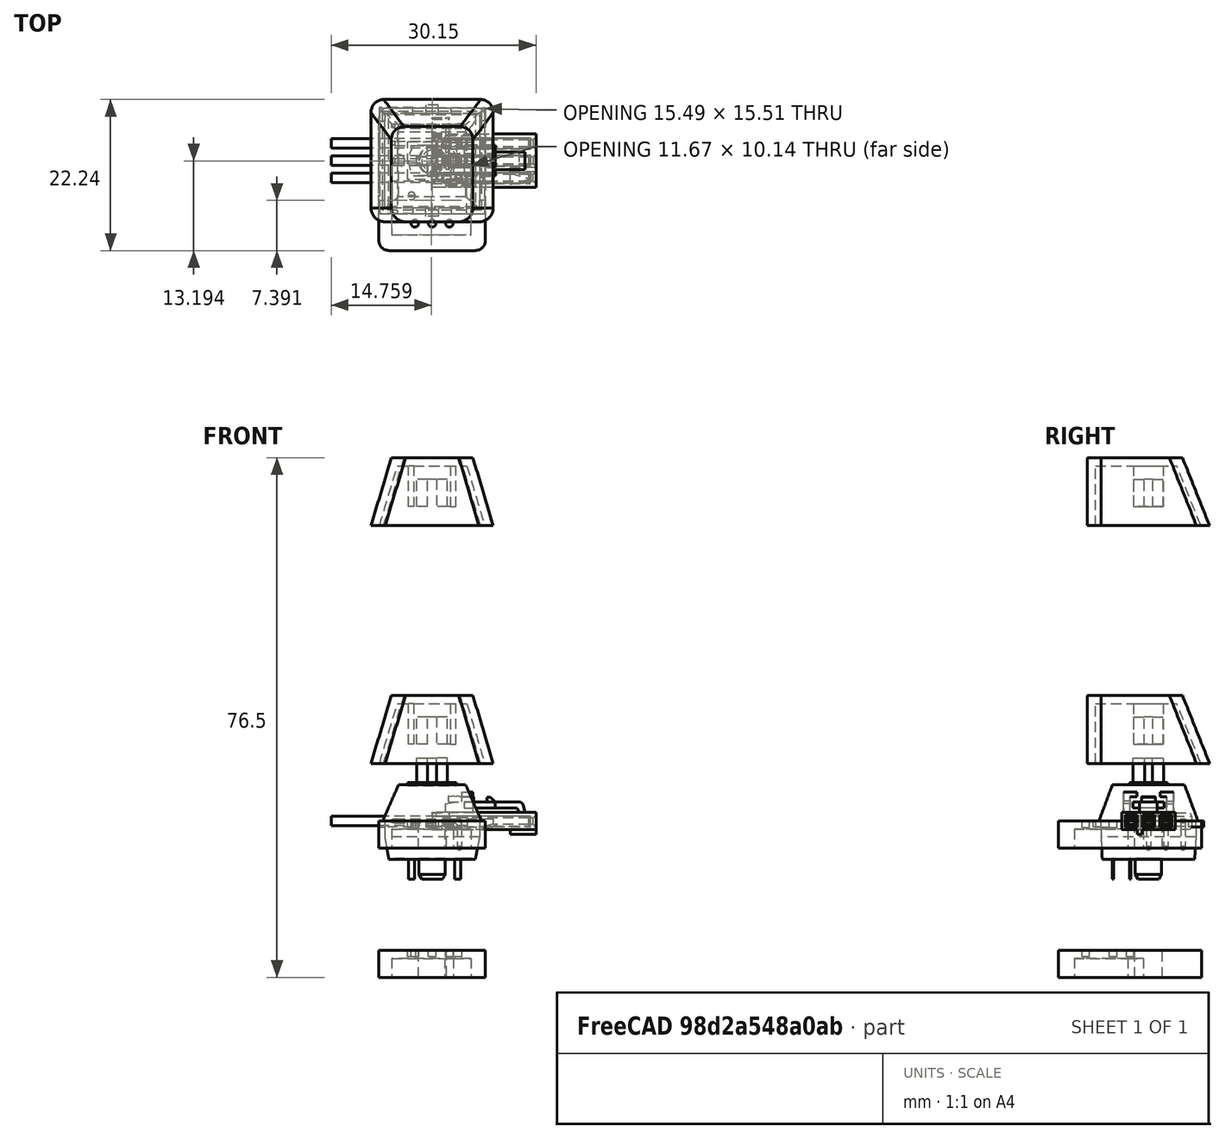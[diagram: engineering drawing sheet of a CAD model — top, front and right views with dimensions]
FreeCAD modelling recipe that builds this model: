
FCSTD DOCUMENT  (FreeCAD 0.19R19285 (Git))
Label: pcbprint-cherry-mx
Comment: 3D-parts by Obijuan -- https://github.com/Obijuan/3D-parts
License: Creative Commons Attribution-ShareAlike
LicenseURL: http://creativecommons.org/licenses/by-sa/4.0/
objects: Part::Feature×36, Part::Part2DObjectPython×33, App::Part×8, Sketcher::SketchObject×6, App::Annotation×5, App::DocumentObjectGroup×4, PartDesign::Pad×2, PartDesign::Pocket×2, PartDesign::Plane×1, PartDesign::Fillet×1, PartDesign::Body×1, Mesh::Feature×1
note: 86 computed .brp shape members not serialized (recipe doc carries the construction recipe); baked Part::Feature solids carry a one-line shape summary decoded from their .brp

FEATURE [Sketcher::SketchObject] Sketch  label="master_h"
  MapMode = 5
  Support = -> [XY_Plane]
  expr: Constraints[1] = 3.8500000000000001 + 0.20000000000000001
  sketch-geometry (14):
    g0: Circle CenterX=0 CenterY=0 CenterZ=0 NormalX=0 NormalY=0 NormalZ=1 AngleXU=0 Radius=2.025
    g1: GeomPoint X=-3.03 Y=-5.2 Z=0
    g2: Circle CenterX=-3.03 CenterY=-5.2 CenterZ=0 NormalX=0 NormalY=0 NormalZ=1 AngleXU=0 Radius=0.55
    g3: GeomPoint X=3.77 Y=-2.7 Z=0
    g4: Circle CenterX=3.77 CenterY=-2.7 CenterZ=0 NormalX=0 NormalY=0 NormalZ=1 AngleXU=0 Radius=0.55
    g5: LineSegment StartX=-7.8514 StartY=7.82934 StartZ=0 EndX=7.8514 EndY=7.82934 EndZ=0
    g6: LineSegment StartX=7.8514 StartY=7.82934 StartZ=0 EndX=7.8514 EndY=-13.2357 EndZ=0
    g7: LineSegment StartX=7.8514 StartY=-13.2357 StartZ=0 EndX=-7.8514 EndY=-13.2357 EndZ=0
    g8: LineSegment StartX=-7.8514 StartY=-13.2357 StartZ=0 EndX=-7.8514 EndY=7.82934 EndZ=0
    g9: Circle CenterX=0 CenterY=-9.23 CenterZ=0 NormalX=0 NormalY=0 NormalZ=1 AngleXU=0 Radius=0.55
    g10: Circle CenterX=2.54 CenterY=-9.23 CenterZ=0 NormalX=0 NormalY=0 NormalZ=1 AngleXU=0 Radius=0.55
    g11: LineSegment [constr] StartX=0 StartY=-9.23 StartZ=0 EndX=2.54 EndY=-9.23 EndZ=0
    g12: Circle CenterX=-2.54 CenterY=-9.23 CenterZ=0 NormalX=0 NormalY=0 NormalZ=1 AngleXU=0 Radius=0.55
    g13: LineSegment [constr] StartX=-2.54 StartY=-9.23 StartZ=0 EndX=0 EndY=-9.23 EndZ=0
  constraints (31):
    c: Coincident(g0,g-1)
    c: Diameter(g0) = 4.05
    c: DistanceX(g1,g0) = 3.03
    c: DistanceY(g1,g0) = 5.2
    c: Coincident(g2,g1)
    c: Diameter(g2) = 1.1
    c: DistanceY(g3,g0) = 2.7
    c: DistanceX(g0,g3) = 3.77
    c: Coincident(g4,g3)
    c: Equal(g2,g4)
    c: Coincident(g5,g6)
    c: Coincident(g6,g7)
    c: Coincident(g7,g8)
    c: Coincident(g8,g5)
    c: Horizontal(g7)
    c: Vertical(g6)
    c: Vertical(g8)
    c: Equal(g2,g9)
    c: PointOnObject(g9,g-2)
    c: DistanceY(g9,g0) = 9.23
    c: Equal(g9,g10)
    c: Coincident(g11,g9)
    c: Coincident(g11,g10)
    c: Horizontal(g11)
    c: DistanceX(g11,g11) = 2.54
    c: Equal(g12,g9)
    c: PointOnObject(g12,g11)
    c: Coincident(g13,g12)
    c: Coincident(g13,g9)
    c: Equal(g13,g11)
    c: Symmetric(g5,g5,g-2)
FEATURE [Sketcher::SketchObject] Sketch001  label="master_v"
  MapMode = 5
  Placement = pos=(0,0,0) rot=(1,0,0;1.5708rad)
  Support = -> [XZ_Plane]
  sketch-geometry (2):
    g0: LineSegment StartX=0 StartY=0 StartZ=0 EndX=0 EndY=-1 EndZ=0
    g1: LineSegment StartX=0 StartY=-1 StartZ=0 EndX=0 EndY=-4 EndZ=0
  constraints (6):
    c: Coincident(g0,g-1)
    c: PointOnObject(g0,g-2)
    c: DistanceY(g0,g0) = 1  'h1'
    c: Coincident(g1,g0)
    c: Vertical(g1)
    c: DistanceY(g1,g1) = 3  'h2'
FEATURE [Sketcher::SketchObject] Sketch002  label="botom_1_sk"
  ExternalGeometry = -> [Sketch]
  MapMode = 5
  Support = -> [XY_Plane]
  sketch-geometry (4):
    g0: LineSegment StartX=-7.8514 StartY=7.82934 StartZ=0 EndX=7.8514 EndY=7.82934 EndZ=0
    g1: LineSegment StartX=7.8514 StartY=7.82934 StartZ=0 EndX=7.8514 EndY=-13.2357 EndZ=0
    g2: LineSegment StartX=7.8514 StartY=-13.2357 StartZ=0 EndX=-7.8514 EndY=-13.2357 EndZ=0
    g3: LineSegment StartX=-7.8514 StartY=-13.2357 StartZ=0 EndX=-7.8514 EndY=7.82934 EndZ=0
  constraints (10):
    c: Coincident(g0,g1)
    c: Coincident(g1,g2)
    c: Coincident(g2,g3)
    c: Coincident(g3,g0)
    c: Horizontal(g0)
    c: Horizontal(g2)
    c: Vertical(g1)
    c: Vertical(g3)
    c: Coincident(g-3,g0)
    c: Coincident(g1,g-4)
FEATURE [PartDesign::Pad] Pad  label="bottom-body"
  Length = 4
  Length2 = 100
  Profile = -> Sketch002
  Refine = true
  Reversed = true
  Type = 0
  expr: Length = <<master_v>>.Constraints.h1 + <<master_v>>.Constraints.h2
FEATURE [Sketcher::SketchObject] Sketch003  label="drills_sk"
  ExternalGeometry = -> [Sketch]
  MapMode = 5
  Support = -> [XY_Plane]
  expr: Constraints[1] = Sketch.Constraints[1]
  expr: Constraints[2] = Sketch.Constraints[2]
  expr: Constraints[5] = Sketch.Constraints[5]
  expr: Constraints[3] = Sketch.Constraints[3]
  expr: Constraints[6] = Sketch.Constraints[6]
  expr: Constraints[7] = Sketch.Constraints[7]
  sketch-geometry (8):
    g0: Circle CenterX=0 CenterY=0 CenterZ=0 NormalX=0 NormalY=0 NormalZ=1 AngleXU=0 Radius=2.025
    g1: GeomPoint X=-3.03 Y=-5.2 Z=0
    g2: Circle CenterX=-3.03 CenterY=-5.2 CenterZ=0 NormalX=0 NormalY=0 NormalZ=1 AngleXU=0 Radius=0.55
    g3: GeomPoint X=3.77 Y=-2.7 Z=0
    g4: Circle CenterX=3.77 CenterY=-2.7 CenterZ=0 NormalX=0 NormalY=0 NormalZ=1 AngleXU=0 Radius=0.55
    g5: Circle CenterX=-2.54 CenterY=-9.23 CenterZ=0 NormalX=0 NormalY=0 NormalZ=1 AngleXU=0 Radius=0.55
    g6: Circle CenterX=0 CenterY=-9.23 CenterZ=0 NormalX=0 NormalY=0 NormalZ=1 AngleXU=0 Radius=0.55
    g7: Circle CenterX=2.54 CenterY=-9.23 CenterZ=0 NormalX=0 NormalY=0 NormalZ=1 AngleXU=0 Radius=0.55
  constraints (16):
    c: Coincident(g0,g-1)
    c: Diameter(g0) = 4.05
    c: DistanceX(g1,g0) = 3.03
    c: DistanceY(g1,g0) = 5.2
    c: Coincident(g2,g1)
    c: Diameter(g2) = 1.1
    c: DistanceY(g3,g0) = 2.7
    c: DistanceX(g0,g3) = 3.77
    c: Coincident(g4,g3)
    c: Equal(g2,g4)
    c: Coincident(g-5,g7)
    c: Equal(g7,g-5)
    c: Coincident(g6,g-4)
    c: Equal(g6,g-4)
    c: Coincident(g5,g-3)
    c: Equal(g5,g-3)
FEATURE [PartDesign::Pocket] Pocket  label="drills-cutout"
  BaseFeature = -> Pad
  Length = 5
  Length2 = 100
  Profile = -> Sketch003
  Refine = true
  Type = 1
FEATURE [Part::Feature] Part__Feature  label="1x3-Insulator"
  shape: bbox 2.54 x 7.62 x 2.5 mm, 30 faces (baked)
FEATURE [Part::Feature] Part__Feature001  label="pin"
  shape: bbox 10.36 x 0.64 x 4.57 mm, 18 faces (baked)
FEATURE [Part::Feature] Part__Feature002  label="pin2"
  Placement = pos=(0,2.54,0) rot=(0,0,1;0rad)
  shape: bbox 10.36 x 0.64 x 4.57 mm, 18 faces (baked)
FEATURE [Part::Feature] Part__Feature003  label="pin3"
  Placement = pos=(0,5.08,0) rot=(0,0,1;0rad)
  shape: bbox 10.36 x 0.64 x 4.57 mm, 18 faces (baked)
FEATURE [App::Part] _x3_mape_pin_header_right_angle  label="1x3-mape-pin-header-right-angle"
  Group = -> [Part__Feature,Part__Feature001,Part__Feature002,Part__Feature003]
  Origin = -> Origin001
  Placement = pos=(2.55,-13.25,1.25) rot=(0,0,1;1.5708rad)
FEATURE [Part::Feature] Part__Feature004  label="cherry-body"
  shape: bbox 15.64 x 16.33 x 10.95 mm, 75 faces (baked)
FEATURE [Part::Feature] Part__Feature005  label="cherry-axis"
  Placement = pos=(0,0,5.25) rot=(0,0,1;0rad)
  shape: bbox 7.2 x 5.56 x 4.05 mm, 19 faces (baked)
FEATURE [Part::Feature] Part__Feature006  label="cherry-peg"
  Placement = pos=(0,0,-8.55) rot=(0,0,1;0rad)
  shape: bbox 3.85 x 3.85 x 3.05 mm, 4 faces (baked)
FEATURE [Part::Feature] Part__Feature007  label="pin1"
  Placement = pos=(-3.03,-5.2,-8.55) rot=(0,0,1;0rad)
  shape: bbox 0.86 x 0.2 x 3.05 mm, 6 faces (baked)
FEATURE [Part::Feature] Part__Feature008  label="pin004"
  Placement = pos=(3.77,-2.7,-8.55) rot=(0,0,1;0rad)
  shape: bbox 0.86 x 0.2 x 3.05 mm, 6 faces (baked)
FEATURE [App::Part] cherry_mx_basic  label="cherry-mx-basic"
  Group = -> [Part__Feature004,Part__Feature005,Part__Feature006,Part__Feature007,Part__Feature008]
  Origin = -> Origin002
  Placement = pos=(0,0,5.6) rot=(0,0,1;0rad)
FEATURE [Part::Feature] Part__Feature016  label="Connector"
  shape: bbox 15.3 x 7.9 x 6.24 mm, 133 faces (baked)
FEATURE [Part::Feature] Part__Feature017  label="pins"
  shape: bbox 12.6 x 1.5 x 1.959 mm, 26 faces (baked)
FEATURE [Part::Feature] Part__Feature018  label="pins001"
  shape: bbox 12.6 x 1.5 x 1.959 mm, 26 faces (baked)
FEATURE [Part::Feature] Part__Feature019  label="pins002"
  shape: bbox 12.6 x 1.5 x 1.959 mm, 26 faces (baked)
FEATURE [App::Part] pins  label="pins003"
  Group = -> [Part__Feature017,Part__Feature018,Part__Feature019]
  Origin = -> Origin004
FEATURE [Part::Feature] Part__Feature020  label="vcc-wire001"
  Placement = pos=(5.15,0,0) rot=(0,-1,0;1.5708rad)
  shape: bbox 20 x 1.4 x 1.4 mm, 3 faces (baked)
FEATURE [Part::Feature] Part__Feature021  label="vcc-signal001"
  Placement = pos=(5.15,2.54,0) rot=(0,-1,0;1.5708rad)
  shape: bbox 20 x 1.4 x 1.4 mm, 3 faces (baked)
FEATURE [Part::Feature] Part__Feature022  label="wire-gnd001"
  Placement = pos=(5.15,-2.54,0) rot=(0,-1,0;1.5708rad)
  shape: bbox 20 x 1.4 x 1.4 mm, 3 faces (baked)
FEATURE [App::Part] ASSEMBLY001  label="female-connector"
  Group = -> [Part__Feature016,pins,Part__Feature020,Part__Feature021,Part__Feature022]
  Origin = -> Origin005
  Placement = pos=(-6.4e-15,-28.7,1.25) rot=(0,0,1;1.5708rad)
FEATURE [PartDesign::Plane] DatumPlane  label="First-layer"
  AttachmentOffset = pos=(0,0,-1) rot=(0,0,1;0rad)
  Length = 60
  MapMode = 2
  Placement = pos=(0,0,-1) rot=(0,0,1;0rad)
  ResizeMode = 0
  Support = -> [XY_Plane]
  Width = 60
FEATURE [Sketcher::SketchObject] Sketch004  label="tracks-sk"
  MapMode = 5
  Placement = pos=(0,0,-1) rot=(0,0,1;0rad)
  Support = -> [DatumPlane]
  sketch-geometry (6):
    g0: LineSegment StartX=-5.92823 StartY=-3.06635 StartZ=0 EndX=1.85452 EndY=-3.06635 EndZ=0
    g1: LineSegment StartX=1.85452 StartY=-3.06635 StartZ=0 EndX=3.12806 EndY=-0.77869 EndZ=0
    g2: LineSegment StartX=3.12806 StartY=-0.77869 StartZ=0 EndX=5.7459 EndY=-0.77869 EndZ=0
    g3: LineSegment StartX=5.7459 StartY=-0.77869 StartZ=0 EndX=5.7459 EndY=-10.9199 EndZ=0
    g4: LineSegment StartX=5.7459 StartY=-10.9199 StartZ=0 EndX=-5.92823 EndY=-10.9199 EndZ=0
    g5: LineSegment StartX=-5.92823 StartY=-10.9199 StartZ=0 EndX=-5.92823 EndY=-3.06635 EndZ=0
  constraints (11):
    c: Horizontal(g0)
    c: Coincident(g0,g1)
    c: Coincident(g1,g2)
    c: Horizontal(g2)
    c: Coincident(g2,g3)
    c: Vertical(g3)
    c: Coincident(g3,g4)
    c: Horizontal(g4)
    c: Coincident(g4,g5)
    c: Coincident(g5,g0)
    c: Vertical(g5)
FEATURE [PartDesign::Pocket] Pocket001  label="tracks-cutout"
  BaseFeature = -> Pocket
  Length = 5
  Length2 = 100
  Profile = -> Sketch004
  Refine = true
  Type = 1
FEATURE [Sketcher::SketchObject] Sketch005  label="drills-fill-sk"
  ExternalGeometry = -> [Sketch004]
  MapMode = 5
  Placement = pos=(0,0,-1) rot=(0,0,1;0rad)
  Support = -> [DatumPlane]
  sketch-geometry (6):
    g0: LineSegment StartX=-5.92823 StartY=-3.06635 StartZ=0 EndX=1.85452 EndY=-3.06635 EndZ=0
    g1: LineSegment StartX=1.85452 StartY=-3.06635 StartZ=0 EndX=3.12806 EndY=-0.77869 EndZ=0
    g2: LineSegment StartX=3.12806 StartY=-0.77869 StartZ=0 EndX=5.7459 EndY=-0.77869 EndZ=0
    g3: LineSegment StartX=5.7459 StartY=-0.77869 StartZ=0 EndX=5.7459 EndY=-10.9199 EndZ=0
    g4: LineSegment StartX=5.7459 StartY=-10.9199 StartZ=0 EndX=-5.92823 EndY=-10.9199 EndZ=0
    g5: LineSegment StartX=-5.92823 StartY=-10.9199 StartZ=0 EndX=-5.92823 EndY=-3.06635 EndZ=0
  constraints (13):
    c: Coincident(g0,g1)
    c: Coincident(g1,g2)
    c: Coincident(g2,g3)
    c: Coincident(g3,g4)
    c: Horizontal(g4)
    c: Coincident(g4,g5)
    c: Coincident(g5,g0)
    c: Vertical(g5)
    c: Coincident(g0,g-3)
    c: Coincident(g0,g-4)
    c: Coincident(g1,g-5)
    c: Coincident(g2,g-6)
    c: Coincident(g3,g-7)
FEATURE [PartDesign::Pad] Pad001  label="drills-fill"
  BaseFeature = -> Pocket001
  Length = 0.2
  Length2 = 100
  Profile = -> Sketch005
  Refine = true
  Reversed = true
  Type = 0
FEATURE [PartDesign::Fillet] Fillet
  Base = -> Pad001 [Edge8,Edge5,Edge2,Edge1]
  BaseFeature = -> Pad001
  Radius = 1.5
FEATURE [PartDesign::Body] Body  label="pcbprint-cherry-mx"
  Group = -> [Sketch,Sketch001,DatumPlane,Sketch002,Pad,Sketch003,Pocket,Sketch004,Pocket001,Pad001,Fillet,Sketch005]
  Origin = -> Origin
  Tip = -> Fillet
FEATURE [Mesh::Feature] Mesh  label="pcbprint-cherry-mx (Meshed)"
FEATURE [Part::Feature] Body001  label="Keycap001"
  Placement = pos=(0,0,8.5) rot=(0,0,1;3.14159rad)
  shape: bbox 26.73 x 25.51 x 16.24 mm, 32 faces (baked)
FEATURE [Part::Feature] Body002  label="pcbprint-cherry-mx001"
  shape: bbox 15.7 x 21.07 x 4 mm, 28 faces (baked)
FEATURE [App::DocumentObjectGroup] Group  label="Assembly"
  Group = -> [_x3_mape_pin_header_right_angle,cherry_mx_basic,ASSEMBLY001,Body001,Body002]
FEATURE [Part::Feature] Body003  label="pcbprint-cherry-mx002"
  Placement = pos=(0,0,-19) rot=(0,0,1;0rad)
  shape: bbox 15.7 x 21.07 x 4 mm, 28 faces (baked)
FEATURE [Part::Feature] Part__Feature023  label="1x3-Insulator001"
  shape: bbox 2.54 x 7.62 x 2.5 mm, 30 faces (baked)
FEATURE [Part::Feature] Part__Feature024  label="pin005"
  shape: bbox 10.36 x 0.64 x 4.57 mm, 18 faces (baked)
FEATURE [Part::Feature] Part__Feature025  label="pin006"
  Placement = pos=(0,2.54,0) rot=(0,0,1;0rad)
  shape: bbox 10.36 x 0.64 x 4.57 mm, 18 faces (baked)
FEATURE [Part::Feature] Part__Feature026  label="pin007"
  Placement = pos=(0,5.08,0) rot=(0,0,1;0rad)
  shape: bbox 10.36 x 0.64 x 4.57 mm, 18 faces (baked)
FEATURE [App::Part] _x3_mape_pin_header_right_angle001  label="1x3-mape-pin-header-right-angle001"
  Group = -> [Part__Feature023,Part__Feature024,Part__Feature025,Part__Feature026]
  Origin = -> Origin006
  Placement = pos=(2.55,-13.25,1.25) rot=(0,0,1;1.5708rad)
FEATURE [Part::Feature] Part__Feature027  label="cherry-body001"
  shape: bbox 15.64 x 16.33 x 10.95 mm, 75 faces (baked)
FEATURE [Part::Feature] Part__Feature028  label="cherry-axis001"
  Placement = pos=(0,0,5.25) rot=(0,0,1;0rad)
  shape: bbox 7.2 x 5.56 x 4.05 mm, 19 faces (baked)
FEATURE [Part::Feature] Part__Feature029  label="cherry-peg001"
  Placement = pos=(0,0,-8.55) rot=(0,0,1;0rad)
  shape: bbox 3.85 x 3.85 x 3.05 mm, 4 faces (baked)
FEATURE [Part::Feature] Part__Feature030  label="pin008"
  Placement = pos=(-3.03,-5.2,-8.55) rot=(0,0,1;0rad)
  shape: bbox 0.86 x 0.2 x 3.05 mm, 6 faces (baked)
FEATURE [Part::Feature] Part__Feature031  label="pin009"
  Placement = pos=(3.77,-2.7,-8.55) rot=(0,0,1;0rad)
  shape: bbox 0.86 x 0.2 x 3.05 mm, 6 faces (baked)
FEATURE [App::Part] cherry_mx_basic001  label="cherry-mx-basic001"
  Group = -> [Part__Feature027,Part__Feature028,Part__Feature029,Part__Feature030,Part__Feature031]
  Origin = -> Origin007
  Placement = pos=(0,0,12.6) rot=(0,0,1;0rad)
FEATURE [Part::Feature] Part__Feature032  label="Connector001"
  shape: bbox 15.3 x 7.9 x 6.24 mm, 133 faces (baked)
FEATURE [Part::Feature] Part__Feature033  label="pins004"
  shape: bbox 12.6 x 1.5 x 1.959 mm, 26 faces (baked)
FEATURE [Part::Feature] Part__Feature034  label="pins005"
  shape: bbox 12.6 x 1.5 x 1.959 mm, 26 faces (baked)
FEATURE [Part::Feature] Part__Feature035  label="pins006"
  shape: bbox 12.6 x 1.5 x 1.959 mm, 26 faces (baked)
FEATURE [App::Part] pins001  label="pins007"
  Group = -> [Part__Feature033,Part__Feature034,Part__Feature035]
  Origin = -> Origin008
FEATURE [Part::Feature] Part__Feature036  label="vcc-wire002"
  Placement = pos=(5.15,0,0) rot=(0,-1,0;1.5708rad)
  shape: bbox 20 x 1.4 x 1.4 mm, 3 faces (baked)
FEATURE [Part::Feature] Part__Feature037  label="vcc-signal002"
  Placement = pos=(5.15,2.54,0) rot=(0,-1,0;1.5708rad)
  shape: bbox 20 x 1.4 x 1.4 mm, 3 faces (baked)
FEATURE [Part::Feature] Part__Feature038  label="wire-gnd002"
  Placement = pos=(5.15,-2.54,0) rot=(0,-1,0;1.5708rad)
  shape: bbox 20 x 1.4 x 1.4 mm, 3 faces (baked)
FEATURE [App::Part] ASSEMBLY002  label="female-connector001"
  Group = -> [Part__Feature032,pins001,Part__Feature036,Part__Feature037,Part__Feature038]
  Origin = -> Origin009
  Placement = pos=(-1.06e-14,-47.7,1.25) rot=(0,0,1;1.5708rad)
FEATURE [Part::Feature] Body004  label="Keycap002"
  Placement = pos=(0,0,43.5) rot=(0,0,1;3.14159rad)
  shape: bbox 26.73 x 25.51 x 16.24 mm, 32 faces (baked)
FEATURE [Part::Part2DObjectPython] Line  # Draft 2D object (typed FeaturePython)
  Area = 0
  ChamferSize = 0
  Closed = false
  End = (0,0,-19)
  FilletRadius = 0
  Length = 23.05
  MakeFace = false
  Placement = pos=(0,0,4.05) rot=(0,0,1;0rad)
  Points = (2) [(0,0,0),(0,0,-23.05)]
  Start = (0,0,4.05)
  Subdivisions = 0
FEATURE [Part::Part2DObjectPython] Line001  # Draft 2D object (typed FeaturePython)
  Area = 0
  ChamferSize = 0
  Closed = false
  End = (2.37,-9.03,-3)
  FilletRadius = 0
  Length = 0.509117
  MakeFace = false
  Placement = pos=(2.73,-9.39,-3) rot=(0,0,1;0rad)
  Points = (2) [(0,0,0),(-0.36,0.36,0)]
  Start = (2.73,-9.39,-3)
  Subdivisions = 0
FEATURE [Part::Part2DObjectPython] Line002  # Draft 2D object (typed FeaturePython)
  Area = 0
  ChamferSize = 0
  Closed = false
  End = (2.54,-9.23,-19)
  FilletRadius = 0
  Length = 16
  MakeFace = false
  Placement = pos=(2.55,-9.21,-3) rot=(0,0,1;0rad)
  Points = (2) [(0,0,0),(-0.01,-0.02,-16)]
  Start = (2.55,-9.21,-3)
  Subdivisions = 0
FEATURE [Part::Part2DObjectPython] Line003  # Draft 2D object (typed FeaturePython)
  Area = 0
  ChamferSize = 0
  Closed = false
  End = (-0.17,-9.03,-3)
  FilletRadius = 0
  Length = 0.509117
  MakeFace = false
  Placement = pos=(0.19,-9.39,-3) rot=(0,0,1;0rad)
  Points = (2) [(0,0,0),(-0.36,0.36,0)]
  Start = (0.19,-9.39,-3)
  Subdivisions = 0
FEATURE [Part::Part2DObjectPython] Line004  # Draft 2D object (typed FeaturePython)
  Area = 0
  ChamferSize = 0
  Closed = false
  End = (0,-9.23,-20)
  FilletRadius = 0
  Length = 17
  MakeFace = false
  Placement = pos=(0.01,-9.21,-3) rot=(0,0,1;0rad)
  Points = (2) [(0,0,0),(-0.01,-0.02,-17)]
  Start = (0.01,-9.21,-3)
  Subdivisions = 0
FEATURE [Part::Part2DObjectPython] Line005  # Draft 2D object (typed FeaturePython)
  Area = 0
  ChamferSize = 0
  Closed = false
  End = (-2.35,-9.03,-3)
  FilletRadius = 0
  Length = 0.509117
  MakeFace = false
  Placement = pos=(-2.71,-9.39,-3) rot=(0,0,1;0rad)
  Points = (2) [(0,0,0),(0.36,0.36,0)]
  Start = (-2.71,-9.39,-3)
  Subdivisions = 0
FEATURE [Part::Part2DObjectPython] Line006  # Draft 2D object (typed FeaturePython)
  Area = 0
  ChamferSize = 0
  Closed = false
  End = (-2.54,-9.23,-20)
  FilletRadius = 0
  Length = 17
  MakeFace = false
  Placement = pos=(-2.53,-9.21,-3) rot=(0,0,1;0rad)
  Points = (2) [(0,0,0),(-0.01,-0.02,-17)]
  Start = (-2.53,-9.21,-3)
  Subdivisions = 0
FEATURE [Part::Part2DObjectPython] Line007  # Draft 2D object (typed FeaturePython)
  Area = 0
  ChamferSize = 0
  Closed = false
  End = (3.34,-2.6,4.05)
  FilletRadius = 0
  Length = 0.88295
  MakeFace = false
  Placement = pos=(4.2,-2.8,4.05) rot=(0,0,1;0rad)
  Points = (2) [(0,0,0),(-0.86,0.2,0)]
  Start = (4.2,-2.8,4.05)
  Subdivisions = 0
FEATURE [Part::Part2DObjectPython] Line008  # Draft 2D object (typed FeaturePython)
  Area = 0
  ChamferSize = 0
  Closed = false
  End = (3.77,-2.7,-20)
  FilletRadius = 0
  Length = 24.05
  MakeFace = false
  Placement = pos=(3.77,-2.7,4.05) rot=(0,0,1;0rad)
  Points = (2) [(0,0,0),(0,0,-24.05)]
  Start = (3.77,-2.7,4.05)
  Subdivisions = 0
FEATURE [Part::Part2DObjectPython] Line009  # Draft 2D object (typed FeaturePython)
  Area = 0
  ChamferSize = 0
  Closed = false
  End = (-3.46,-5.1,4.05)
  FilletRadius = 0
  Length = 0.88295
  MakeFace = false
  Placement = pos=(-2.6,-5.3,4.05) rot=(0,0,1;0rad)
  Points = (2) [(0,0,0),(-0.86,0.2,0)]
  Start = (-2.6,-5.3,4.05)
  Subdivisions = 0
FEATURE [Part::Part2DObjectPython] Line010  # Draft 2D object (typed FeaturePython)
  Area = 0
  ChamferSize = 0
  Closed = false
  End = (-3.03,-5.2,-20)
  FilletRadius = 0
  Length = 24.05
  MakeFace = false
  Placement = pos=(-3.03,-5.2,4.05) rot=(0,0,1;0rad)
  Points = (2) [(0,0,0),(0,0,-24.05)]
  Start = (-3.03,-5.2,4.05)
  Subdivisions = 0
FEATURE [Part::Part2DObjectPython] Line012  # Draft 2D object (typed FeaturePython)
  Area = 0
  ChamferSize = 0
  Closed = false
  End = (-0.675,0.575,21.9)
  FilletRadius = 0
  Length = 1.77341
  MakeFace = false
  Placement = pos=(0.675,-0.575,21.9) rot=(0,0,1;0rad)
  Points = (2) [(0,0,0),(-1.35,1.15,0)]
  Start = (0.675,-0.575,21.9)
  Subdivisions = 0
FEATURE [Part::Part2DObjectPython] Line013  # Draft 2D object (typed FeaturePython)
  Area = 0
  ChamferSize = 0
  Closed = false
  End = (-0.65,0.65,46.3)
  FilletRadius = 0
  Length = 1.83848
  MakeFace = false
  Placement = pos=(0.65,-0.65,46.3) rot=(0,0,1;0rad)
  Points = (2) [(0,0,0),(-1.3,1.3,0)]
  Start = (0.65,-0.65,46.3)
  Subdivisions = 0
FEATURE [Part::Part2DObjectPython] Line014  # Draft 2D object (typed FeaturePython)
  Area = 0
  ChamferSize = 0
  Closed = false
  End = (0,0,21.9)
  FilletRadius = 0
  Length = 24.4
  MakeFace = false
  Placement = pos=(0,0,46.3) rot=(0,0,1;0rad)
  Points = (2) [(0,0,0),(0,0,-24.4)]
  Start = (0,0,46.3)
  Subdivisions = 0
FEATURE [App::Annotation] Text
  LabelText = 1
  Position = (29,0,59)
FEATURE [Part::Part2DObjectPython] Circle  # Draft 2D object (typed FeaturePython)
  Area = 0
  FirstAngle = 0
  LastAngle = 0
  MakeFace = false
  Placement = pos=(31,0,61) rot=(1,0,0;1.5708rad)
  Radius = 4.24264
FEATURE [Part::Part2DObjectPython] Wire  # Draft 2D object (typed FeaturePython)
  Area = 0
  ChamferSize = 0
  Closed = false
  End = (26.567,0,60.7624)
  FilletRadius = 0
  Length = 23.5533
  MakeFace = false
  Placement = pos=(7.21521,0,51.0103) rot=(1,0,0;1.5708rad)
  Points = (3) [(0,0,0),(9.78479,9.98966,1.91858e-15),(19.3518,9.75206,1.57292e-15)]
  Start = (7.21521,0,51.0103)
  Subdivisions = 0
FEATURE [App::Annotation] Text001
  LabelText = 2
  Position = (29,0,25)
FEATURE [Part::Part2DObjectPython] Circle001  # Draft 2D object (typed FeaturePython)
  Area = 0
  FirstAngle = 0
  LastAngle = 0
  MakeFace = false
  Placement = pos=(31,0,27) rot=(1,0,0;1.5708rad)
  Radius = 5
FEATURE [Part::Part2DObjectPython] Wire001  # Draft 2D object (typed FeaturePython)
  Area = 0
  ChamferSize = 0
  Closed = false
  End = (25.757,0,27.0144)
  FilletRadius = 0
  Length = 24.2127
  MakeFace = false
  Placement = pos=(5.94809,0,16.1957) rot=(1,0,0;1.5708rad)
  Points = (3) [(0,0,0),(11.0519,10.8043,2.06068e-15),(19.8089,10.8187,1.79576e-15)]
  Start = (5.94809,0,16.1957)
  Subdivisions = 0
FEATURE [App::Annotation] Text002
  LabelText = 3
  Position = (30,0,-11)
FEATURE [Part::Part2DObjectPython] Circle002  # Draft 2D object (typed FeaturePython)
  Area = 0
  FirstAngle = 0
  LastAngle = 0
  MakeFace = false
  Placement = pos=(31,0,-9) rot=(1,0,0;1.5708rad)
  Radius = 4.91184
FEATURE [Part::Part2DObjectPython] Wire002  # Draft 2D object (typed FeaturePython)
  Area = 0
  ChamferSize = 0
  Closed = false
  End = (25.9814,0,-8.25937)
  FilletRadius = 0
  Length = 23.0922
  MakeFace = false
  Placement = pos=(7.54392,0,-18.4686) rot=(1,0,0;1.5708rad)
  Points = (3) [(0,0,0),(9.45608,10.4686,2.03498e-15),(18.4375,10.2092,1.70241e-15)]
  Start = (7.54392,0,-18.4686)
  Subdivisions = 0
FEATURE [App::Annotation] Text003
  LabelText = 4
  Position = (-35,0,-6)
FEATURE [Part::Part2DObjectPython] Circle003  # Draft 2D object (typed FeaturePython)
  Area = 0
  FirstAngle = 0
  LastAngle = 0
  MakeFace = false
  Placement = pos=(-33,0,-4) rot=(1,0,0;1.5708rad)
  Radius = 4.24264
FEATURE [Part::Part2DObjectPython] Wire003  # Draft 2D object (typed FeaturePython)
  Area = 0
  ChamferSize = 0
  Closed = false
  End = (-14.1856,0,-8.36503)
  FilletRadius = 0
  Length = 16.5453
  MakeFace = false
  Placement = pos=(-28.3446,0,-4.39854) rot=(1,0,0;1.5708rad)
  Points = (3) [(0,0,0),(11.3446,0.398539,-2.58835e-16),(14.159,-3.96649,-1.31423e-15)]
  Start = (-28.3446,0,-4.39854)
  Subdivisions = 0
FEATURE [App::Annotation] Text004
  LabelText = 5
  Position = (-57,0,-29)
FEATURE [Part::Part2DObjectPython] Circle004  # Draft 2D object (typed FeaturePython)
  Area = 0
  FirstAngle = 0
  LastAngle = 0
  MakeFace = false
  Placement = pos=(-56,0,-27) rot=(1,0,0;1.5708rad)
  Radius = 4.12311
FEATURE [Part::Part2DObjectPython] Wire004  # Draft 2D object (typed FeaturePython)
  Area = 0
  ChamferSize = 0
  Closed = false
  End = (-39.1448,0,-32.2391)
  FilletRadius = 0
  Length = 15.7049
  MakeFace = false
  Placement = pos=(-51.8883,0,-28.0282) rot=(1,0,0;1.5708rad)
  Points = (4) [(0,0,0),(10.8883,0.0281517,-3.27106e-16),(12.9181,-4.12362,-1.31113e-15),(12.7435,-4.2109,-1.32516e-15)]
  Start = (-51.8883,0,-28.0282)
  Subdivisions = 0
FEATURE [Part::Part2DObjectPython] Line015  # Draft 2D object (typed FeaturePython)
  Area = 0
  ChamferSize = 0
  Closed = false
  End = (-1.64,-32.4,0.35)
  FilletRadius = 0
  Length = 2.54558
  MakeFace = false
  Placement = pos=(-3.44,-32.4,2.15) rot=(0,0,1;0rad)
  Points = (2) [(0,0,0),(1.8,0,-1.8)]
  Start = (-3.44,-32.4,2.15)
  Subdivisions = 0
FEATURE [Part::Part2DObjectPython] Line016  # Draft 2D object (typed FeaturePython)
  Area = 0
  ChamferSize = 0
  Closed = false
  End = (0.9,-32.4,0.35)
  FilletRadius = 0
  Length = 2.54558
  MakeFace = false
  Placement = pos=(-0.9,-32.4,2.15) rot=(0,0,1;0rad)
  Points = (2) [(0,0,0),(1.8,0,-1.8)]
  Start = (-0.9,-32.4,2.15)
  Subdivisions = 0
FEATURE [Part::Part2DObjectPython] Line017  # Draft 2D object (typed FeaturePython)
  Area = 0
  ChamferSize = 0
  Closed = false
  End = (3.44,-32.4,0.35)
  FilletRadius = 0
  Length = 2.54558
  MakeFace = false
  Placement = pos=(1.64,-32.4,2.15) rot=(0,0,1;0rad)
  Points = (2) [(0,0,0),(1.8,0,-1.8)]
  Start = (1.64,-32.4,2.15)
  Subdivisions = 0
FEATURE [Part::Part2DObjectPython] Line018  # Draft 2D object (typed FeaturePython)
  Area = 0
  ChamferSize = 0
  Closed = false
  End = (-2.35,-19.25,1.07)
  FilletRadius = 0
  Length = 0.509117
  MakeFace = false
  Placement = pos=(-2.71,-19.25,1.43) rot=(0,0,1;0rad)
  Points = (2) [(0,0,0),(0.36,0,-0.36)]
  Start = (-2.71,-19.25,1.43)
  Subdivisions = 0
FEATURE [Part::Part2DObjectPython] Line019  # Draft 2D object (typed FeaturePython)
  Area = 0
  ChamferSize = 0
  Closed = false
  End = (0.19,-19.25,1.07)
  FilletRadius = 0
  Length = 0.509117
  MakeFace = false
  Placement = pos=(-0.17,-19.25,1.43) rot=(0,0,1;0rad)
  Points = (2) [(0,0,0),(0.36,0,-0.36)]
  Start = (-0.17,-19.25,1.43)
  Subdivisions = 0
FEATURE [Part::Part2DObjectPython] Line020  # Draft 2D object (typed FeaturePython)
  Area = 0
  ChamferSize = 0
  Closed = false
  End = (2.73,-19.25,1.07)
  FilletRadius = 0
  Length = 0.509117
  MakeFace = false
  Placement = pos=(2.37,-19.25,1.43) rot=(0,0,1;0rad)
  Points = (2) [(0,0,0),(0.36,0,-0.36)]
  Start = (2.37,-19.25,1.43)
  Subdivisions = 0
FEATURE [Part::Part2DObjectPython] Line021  # Draft 2D object (typed FeaturePython)
  Area = 0
  ChamferSize = 0
  Closed = false
  End = (2.54,-32.4,1.25)
  FilletRadius = 0
  Length = 13.15
  MakeFace = false
  Placement = pos=(2.55,-19.25,1.25) rot=(0,0,1;0rad)
  Points = (2) [(0,0,0),(-0.01,-13.15,0)]
  Start = (2.55,-19.25,1.25)
  Subdivisions = 0
FEATURE [Part::Part2DObjectPython] Line022  # Draft 2D object (typed FeaturePython)
  Area = 0
  ChamferSize = 0
  Closed = false
  End = (-7.1e-15,-32.4,1.25)
  FilletRadius = 0
  Length = 13.15
  MakeFace = false
  Placement = pos=(0.01,-19.25,1.25) rot=(0,0,1;0rad)
  Points = (2) [(0,0,0),(-0.01,-13.15,0)]
  Start = (0.01,-19.25,1.25)
  Subdivisions = 0
FEATURE [Part::Part2DObjectPython] Line023  # Draft 2D object (typed FeaturePython)
  Area = 0
  ChamferSize = 0
  Closed = false
  End = (-2.54,-32.4,1.25)
  FilletRadius = 0
  Length = 13.15
  MakeFace = false
  Placement = pos=(-2.53,-19.25,1.25) rot=(0,0,1;0rad)
  Points = (2) [(0,0,0),(-0.01,-13.15,0)]
  Start = (-2.53,-19.25,1.25)
  Subdivisions = 0
FEATURE [App::DocumentObjectGroup] Group001  label="Exploded-view"
  Group = -> [_x3_mape_pin_header_right_angle001,cherry_mx_basic001,ASSEMBLY002,Body004,Body003,Line,Line001,Line002,Line003,Line004,Line005,Line006,Line007,Line008,Line009,Line010,Line012,Line013,Line014,Text,Circle,Wire,Text001,Circle001,Wire001,Text002,Circle002,Wire002,Text003,Circle003,Wire003,Text004,Circle004,Wire004,Line015,Line016,Line017,Line018,Line019,Line020,Line021,Line022,Line023]
FEATURE [App::DocumentObjectGroup] Group002  label="Modelo-imprimible"
  Group = -> [Mesh]
FEATURE [App::DocumentObjectGroup] Group003  label="src"
  Group = -> [Body]
